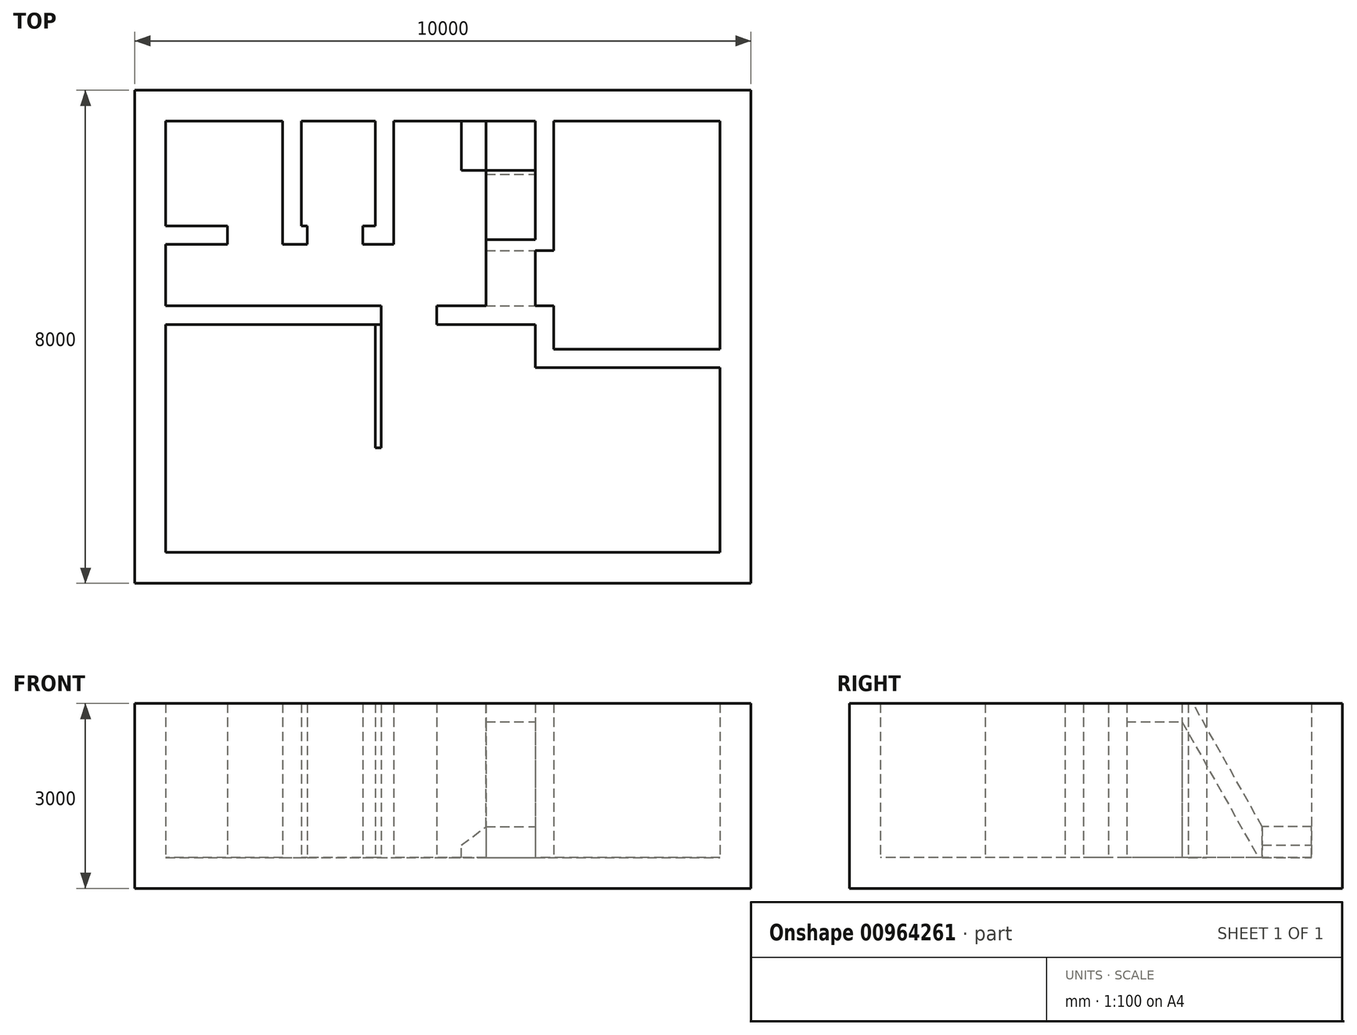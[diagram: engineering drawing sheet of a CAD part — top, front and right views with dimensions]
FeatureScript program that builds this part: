
annotation { "Feature Type Name" : "Feature", "Feature Type Description" : "" }
export const myFeature = defineFeature(function(context is Context, id is Id, definition is map)
    precondition{}
    {
        {
            var Q0;
            Q0=qCreatedBy(makeId("Top.planeOp"),FACE);
            var sketch = newSketch(context, id + "F0", { "sketchPlane" : qUnion([Q0])});
            skLineSegment(sketch, "E0.bottom", {"start": v(0, 0) * mm, "end": v(-10000, 0) * mm});
            skLineSegment(sketch, "E0.right", {"start": v(-10000, 0) * mm, "end": v(-10000, -8000) * mm});
            skPoint(sketch, "E0.middle", {"position": v(0, 0) * mm});
            skLineSegment(sketch, "E1.top", {"start": v(-10000, -8000) * mm, "end": v(0, -8000) * mm});
            skLineSegment(sketch, "E1.right", {"start": v(0, 0) * mm, "end": v(0, -8000) * mm});
            skSolve(sketch);
        }
        {
            var Q0;
            Q0 = qSketchRegion(id + "F0", true);
            extrude(context, id + "F1", {"entities" : qUnion([Q0]), "depth" : 3000 * mm, "offsetDistance" : 25 * mm});
        }
        {
            var Q0;
            Q0=makeQuery(id+"F1.opExtrude","CAP_FACE",FACE,{"disambiguationData":[OSD([sQuery(id+"F0.wireOp",EDGE,"E0.bottom"),sQuery(id+"F0.wireOp",EDGE,"E0.top"),sQuery(id+"F0.wireOp",EDGE,"E0.right"),sQuery(id+"F0.wireOp",EDGE,"E1.top"),sQuery(id+"F0.wireOp",EDGE,"E1.left"),sQuery(id+"F0.wireOp",EDGE,"E1.right")])],"isStart":false});
            shell(context, id + "F2", {"entities" : qUnion([Q0]), "thickness" : 500 * mm});
        }
        {
            var Q0;
            Q0=makeQuery(id+"F2.opShell","OFFSET_FACE",FACE,{"disambiguationData":[OSD([sQuery(id+"F0.wireOp",EDGE,"E0.bottom"),sQuery(id+"F0.wireOp",EDGE,"E0.top"),sQuery(id+"F0.wireOp",EDGE,"E0.right"),sQuery(id+"F0.wireOp",EDGE,"E1.top"),sQuery(id+"F0.wireOp",EDGE,"E1.left"),sQuery(id+"F0.wireOp",EDGE,"E1.right")])]});
            var sketch = newSketch(context, id + "F3", { "sketchPlane" : qUnion([Q0])});
            skLineSegment(sketch, "E2", {"start": v(-9500, -3500) * mm, "end": v(-6000, -3500) * mm});
            skLineSegment(sketch, "E3", {"start": v(-6000, -3500) * mm, "end": v(-6000, -3800) * mm});
            skLineSegment(sketch, "E4", {"start": v(-6000, -3800) * mm, "end": v(-9500, -3800) * mm});
            skLineSegment(sketch, "E5", {"start": v(-9500, -3800) * mm, "end": v(-9500, -3500) * mm});
            skLineSegment(sketch, "E6.bottom", {"start": v(-500, -4500) * mm, "end": v(-3500, -4500) * mm});
            skLineSegment(sketch, "E6.top", {"start": v(-500, -4200) * mm, "end": v(-3200, -4200) * mm});
            skLineSegment(sketch, "E6.left", {"start": v(-500, -4500) * mm, "end": v(-500, -4200) * mm});
            skLineSegment(sketch, "E7", {"start": v(-5100, -3800) * mm, "end": v(-3500, -3800) * mm});
            skLineSegment(sketch, "E8", {"start": v(-3500, -3800) * mm, "end": v(-3500, -4500) * mm});
            skLineSegment(sketch, "E9", {"start": v(-5100, -3800) * mm, "end": v(-5100, -3500) * mm});
            skLineSegment(sketch, "E10", {"start": v(-5100, -3500) * mm, "end": v(-3200, -3500) * mm});
            skLineSegment(sketch, "E11", {"start": v(-3200, -3500) * mm, "end": v(-3200, -4200) * mm});
            skLineSegment(sketch, "E12.bottom", {"start": v(-3500, -500) * mm, "end": v(-3200, -500) * mm});
            skLineSegment(sketch, "E12.top", {"start": v(-3500, -2600) * mm, "end": v(-3200, -2600) * mm});
            skLineSegment(sketch, "E12.left", {"start": v(-3500, -500) * mm, "end": v(-3500, -2600) * mm});
            skLineSegment(sketch, "E12.right", {"start": v(-3200, -500) * mm, "end": v(-3200, -2600) * mm});
            skLineSegment(sketch, "E13.bottom", {"start": v(-7600, -500) * mm, "end": v(-7300, -500) * mm});
            skLineSegment(sketch, "E13.top", {"start": v(-7600, -2500) * mm, "end": v(-7200, -2500) * mm});
            skLineSegment(sketch, "E13.left", {"start": v(-7600, -500) * mm, "end": v(-7600, -2500) * mm});
            skLineSegment(sketch, "E14.bottom", {"start": v(-9500, -2500) * mm, "end": v(-8500, -2500) * mm});
            skLineSegment(sketch, "E14.top", {"start": v(-9500, -2200) * mm, "end": v(-8500, -2200) * mm});
            skLineSegment(sketch, "E14.left", {"start": v(-9500, -2500) * mm, "end": v(-9500, -2200) * mm});
            skLineSegment(sketch, "E14.right", {"start": v(-8500, -2500) * mm, "end": v(-8500, -2200) * mm});
            skLineSegment(sketch, "E15.bottom", {"start": v(-6100, -500) * mm, "end": v(-5800, -500) * mm});
            skLineSegment(sketch, "E15.top", {"start": v(-6300, -2500) * mm, "end": v(-5800, -2500) * mm});
            skLineSegment(sketch, "E15.right", {"start": v(-5800, -500) * mm, "end": v(-5800, -2500) * mm});
            skLineSegment(sketch, "E16.left", {"start": v(-7200, -2500) * mm, "end": v(-7200, -2200) * mm});
            skLineSegment(sketch, "E16.right", {"start": v(-6300, -2500) * mm, "end": v(-6300, -2200) * mm});
            skLineSegment(sketch, "E17", {"start": v(-7200, -2200) * mm, "end": v(-7300, -2200) * mm});
            skLineSegment(sketch, "E18", {"start": v(-7300, -2200) * mm, "end": v(-7300, -500) * mm});
            skLineSegment(sketch, "E19", {"start": v(-6100, -500) * mm, "end": v(-6100, -2200) * mm});
            skLineSegment(sketch, "E20", {"start": v(-6100, -2200) * mm, "end": v(-6300, -2200) * mm});
            skSolve(sketch);
        }
        {
            var Q0;
            Q0 = qSketchRegion(id + "F3", true);
            var Q1;
            Q1=makeQuery(id+"F1.opExtrude","CAP_FACE",FACE,{"disambiguationData":[OSD([sQuery(id+"F0.wireOp",EDGE,"E0.bottom"),sQuery(id+"F0.wireOp",EDGE,"E0.top"),sQuery(id+"F0.wireOp",EDGE,"E0.right"),sQuery(id+"F0.wireOp",EDGE,"E1.top"),sQuery(id+"F0.wireOp",EDGE,"E1.left"),sQuery(id+"F0.wireOp",EDGE,"E1.right")])],"isStart":false});
            extrude(context, id + "F4", {"entities" : qUnion([Q0]), "operationType" : NewBodyOperationType.ADD, "endBound" : BoundingType.UP_TO_SURFACE, "depth" : 25 * mm, "endBoundEntityFace" : qUnion([Q1]), "offsetDistance" : 25 * mm});
        }
        {
            var Q0;
            Q0=makeQuery(id+"F2.opShell","OFFSET_FACE",FACE,{"disambiguationData":[OSD([sQuery(id+"F0.wireOp",EDGE,"E0.bottom"),sQuery(id+"F0.wireOp",EDGE,"E0.top"),sQuery(id+"F0.wireOp",EDGE,"E0.right"),sQuery(id+"F0.wireOp",EDGE,"E1.top"),sQuery(id+"F0.wireOp",EDGE,"E1.left"),sQuery(id+"F0.wireOp",EDGE,"E1.right")])]});
            var sketch = newSketch(context, id + "F5", { "sketchPlane" : qUnion([Q0])});
            skLineSegment(sketch, "E21.bottom", {"start": v(-6000, -3800) * mm, "end": v(-6100, -3800) * mm});
            skLineSegment(sketch, "E21.top", {"start": v(-6000, -5800) * mm, "end": v(-6100, -5800) * mm});
            skLineSegment(sketch, "E21.left", {"start": v(-6000, -3800) * mm, "end": v(-6000, -5800) * mm});
            skLineSegment(sketch, "E21.right", {"start": v(-6100, -3800) * mm, "end": v(-6100, -5800) * mm});
            skSolve(sketch);
        }
        {
            var Q0;
            Q0 = qSketchRegion(id + "F5", true);
            var Q1;
            Q1=makeQuery(id+"F4.boolean.opBoolean","MERGE",FACE,{"derivedFrom":[makeQuery(id+"F1.opExtrude","CAP_FACE",FACE,{"disambiguationData":[OSD([sQuery(id+"F0.wireOp",EDGE,"E0.bottom"),sQuery(id+"F0.wireOp",EDGE,"E0.top"),sQuery(id+"F0.wireOp",EDGE,"E0.right"),sQuery(id+"F0.wireOp",EDGE,"E1.top"),sQuery(id+"F0.wireOp",EDGE,"E1.left"),sQuery(id+"F0.wireOp",EDGE,"E1.right")])],"isStart":false}),makeQuery(id+"F4.opExtrude","CAP_FACE",FACE,{"disambiguationData":[OSD([sQuery(id+"F3.wireOp",EDGE,"E2"),sQuery(id+"F3.wireOp",EDGE,"E3"),sQuery(id+"F3.wireOp",EDGE,"E4"),sQuery(id+"F3.wireOp",EDGE,"E5")])],"isStart":false}),makeQuery(id+"F4.opExtrude","CAP_FACE",FACE,{"disambiguationData":[OSD([sQuery(id+"F3.wireOp",EDGE,"E6.bottom"),sQuery(id+"F3.wireOp",EDGE,"E6.top"),sQuery(id+"F3.wireOp",EDGE,"E6.left"),sQuery(id+"F3.wireOp",EDGE,"E7"),sQuery(id+"F3.wireOp",EDGE,"E8"),sQuery(id+"F3.wireOp",EDGE,"E9"),sQuery(id+"F3.wireOp",EDGE,"E10"),sQuery(id+"F3.wireOp",EDGE,"E11")])],"isStart":false}),makeQuery(id+"F4.opExtrude","CAP_FACE",FACE,{"disambiguationData":[OSD([sQuery(id+"F3.wireOp",EDGE,"E12.bottom"),sQuery(id+"F3.wireOp",EDGE,"E12.top"),sQuery(id+"F3.wireOp",EDGE,"E12.left"),sQuery(id+"F3.wireOp",EDGE,"E12.right")])],"isStart":false}),makeQuery(id+"F4.opExtrude","CAP_FACE",FACE,{"disambiguationData":[OSD([sQuery(id+"F3.wireOp",EDGE,"E13.bottom"),sQuery(id+"F3.wireOp",EDGE,"E13.top"),sQuery(id+"F3.wireOp",EDGE,"E13.left"),sQuery(id+"F3.wireOp",EDGE,"E16.left"),sQuery(id+"F3.wireOp",EDGE,"E17"),sQuery(id+"F3.wireOp",EDGE,"E18")])],"isStart":false}),makeQuery(id+"F4.opExtrude","CAP_FACE",FACE,{"disambiguationData":[OSD([sQuery(id+"F3.wireOp",EDGE,"E14.bottom"),sQuery(id+"F3.wireOp",EDGE,"E14.top"),sQuery(id+"F3.wireOp",EDGE,"E14.left"),sQuery(id+"F3.wireOp",EDGE,"E14.right")])],"isStart":false}),makeQuery(id+"F4.opExtrude","CAP_FACE",FACE,{"disambiguationData":[OSD([sQuery(id+"F3.wireOp",EDGE,"E15.bottom"),sQuery(id+"F3.wireOp",EDGE,"E15.top"),sQuery(id+"F3.wireOp",EDGE,"E15.right"),sQuery(id+"F3.wireOp",EDGE,"E16.right"),sQuery(id+"F3.wireOp",EDGE,"E19"),sQuery(id+"F3.wireOp",EDGE,"E20")])],"isStart":false})]});
            extrude(context, id + "F6", {"entities" : qUnion([Q0]), "endBound" : BoundingType.UP_TO_SURFACE, "depth" : 25 * mm, "endBoundEntityFace" : qUnion([Q1]), "offsetDistance" : 25 * mm});
        }
        {
            var Q0;
            Q0=makeQuery(id+"F4.opExtrude","SWEPT_FACE",FACE,{"disambiguationData":[OSD([sQuery(id+"F3.wireOp",EDGE,"E12.left")])]});
            var sketch = newSketch(context, id + "F7", { "sketchPlane" : qUnion([Q0])});
            skLineSegment(sketch, "E22", {"start": v(500, 500) * mm, "end": v(500, 1000) * mm});
            skLineSegment(sketch, "E23", {"start": v(500, 1000) * mm, "end": v(1300, 1000) * mm});
            skLineSegment(sketch, "E24", {"start": v(1300, 1000) * mm, "end": v(2424.5, 3000) * mm});
            skLineSegment(sketch, "E25", {"start": v(2424.5, 3000) * mm, "end": v(3500, 3000) * mm});
            skLineSegment(sketch, "E26", {"start": v(3500, 3000) * mm, "end": v(3500, 2700) * mm});
            skLineSegment(sketch, "E27", {"start": v(3500, 2700) * mm, "end": v(2600, 2700) * mm});
            skLineSegment(sketch, "E28", {"start": v(2600, 2700) * mm, "end": v(1363.04, 500) * mm});
            skLineSegment(sketch, "E29", {"start": v(1363.04, 500) * mm, "end": v(500, 500) * mm});
            skSolve(sketch);
        }
        {
            var Q0;
            Q0 = qSketchRegion(id + "F7", true);
            extrude(context, id + "F8", {"entities" : qUnion([Q0]), "depth" : 800 * mm, "offsetDistance" : 25 * mm});
        }
        {
            var Q0;
            {var subQ6=sQuery(id+"F0.wireOp",EDGE,"E0.bottom");var subQ7=sQuery(id+"F3.wireOp",EDGE,"E12.left");Q0=makeQuery(id+"F4.boolean.opBoolean","SPLIT",FACE,{"disambiguationData":[TD([makeQuery(id+"F4.opExtrude","SWEPT_FACE",FACE,{"disambiguationData":[OSD([subQ7])]})])],"derivedFrom":makeQuery(id+"F2.opShell","OFFSET_FACE",FACE,{"disambiguationData":[OSD([subQ6])]})});}
            var sketch = newSketch(context, id + "F9", { "sketchPlane" : qUnion([Q0])});
            skLineSegment(sketch, "E30", {"start": v(-4300, 1000) * mm, "end": v(-4300, 500) * mm});
            skLineSegment(sketch, "E31", {"start": v(-4300, 500) * mm, "end": v(-4700, 500) * mm});
            skLineSegment(sketch, "E32", {"start": v(-4700, 500) * mm, "end": v(-4700, 700) * mm});
            skLineSegment(sketch, "E33", {"start": v(-4700, 700) * mm, "end": v(-4300, 1000) * mm});
            skSolve(sketch);
        }
        {
            var Q0;
            Q0 = qSketchRegion(id + "F9", true);
            extrude(context, id + "F10", {"entities" : qUnion([Q0]), "operationType" : NewBodyOperationType.ADD, "depth" : 800 * mm, "offsetDistance" : 25 * mm});
        }
    });
